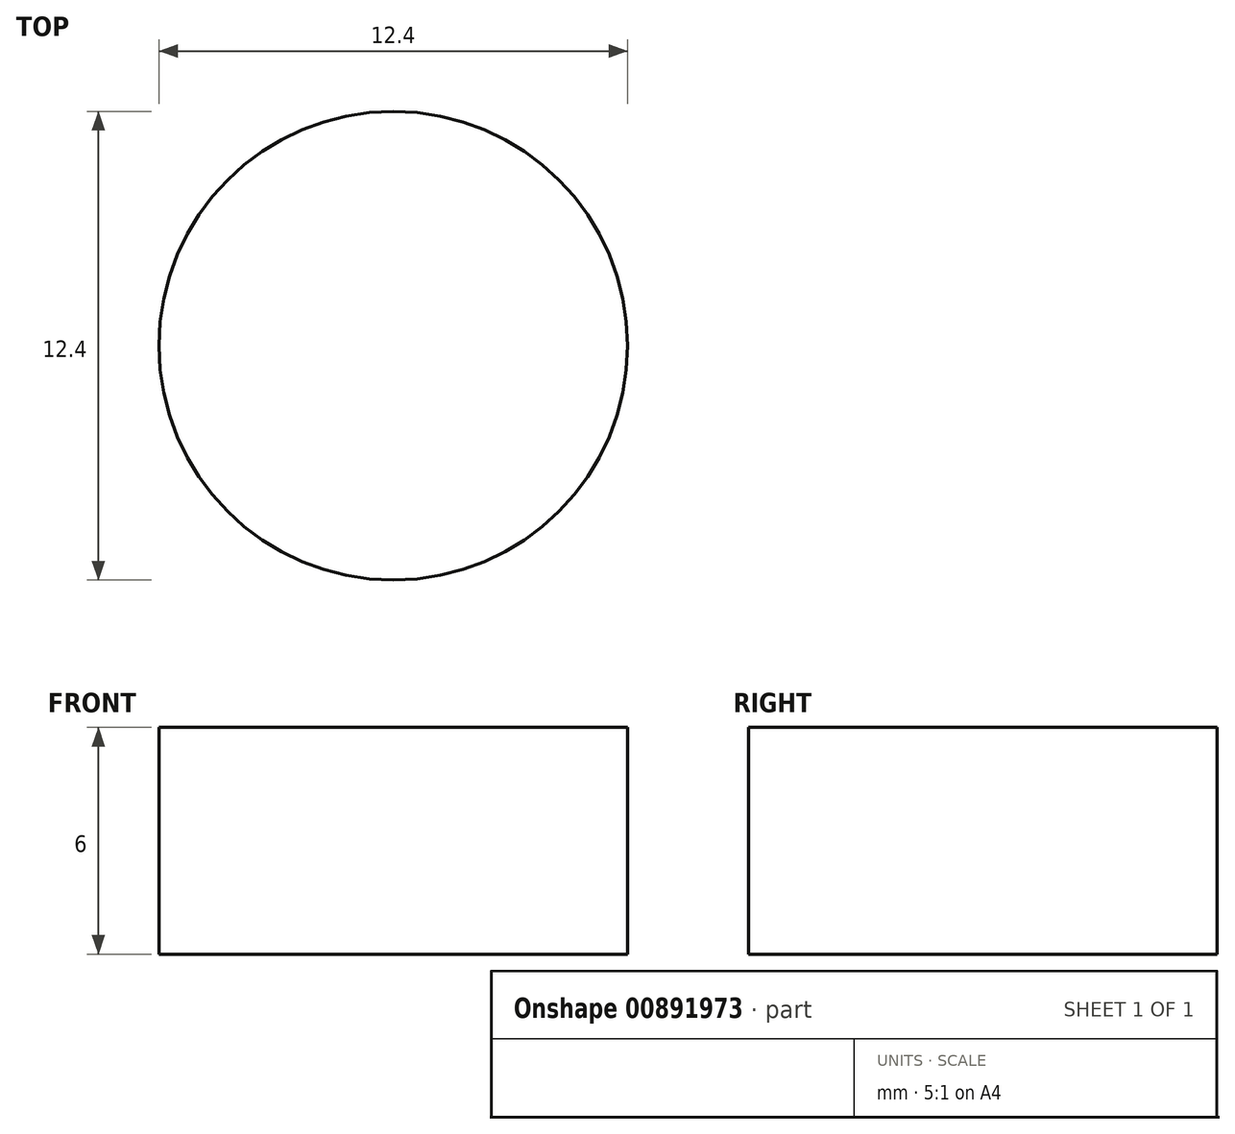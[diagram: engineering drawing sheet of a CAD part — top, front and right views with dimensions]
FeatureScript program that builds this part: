
annotation { "Feature Type Name" : "Feature", "Feature Type Description" : "" }
export const myFeature = defineFeature(function(context is Context, id is Id, definition is map)
    precondition{}
    {
        {
            var Q0;
            Q0=qCreatedBy(makeId("Top.planeOp"),FACE);
            var sketch = newSketch(context, id + "F0", { "sketchPlane" : qUnion([Q0])});
            skCircle(sketch, "E0", {"center": v(0, 0) * mm, "radius": 6.2 * mm});
            skSolve(sketch);
        }
        {
            var Q0;
            Q0=makeQuery(id+"F0.imprint","IMPRINT",FACE,{"disambiguationData":[TD([[makeQuery(id+"F0.imprint","IMPRINT",EDGE,{"derivedFrom":sQuery(id+"F0.wireOp",EDGE,"E0")}),1.0]])]});
            extrude(context, id + "F1", {"entities" : qUnion([Q0]), "depth" : 6 * mm, "offsetDistance" : 25 * mm});
        }
    });
